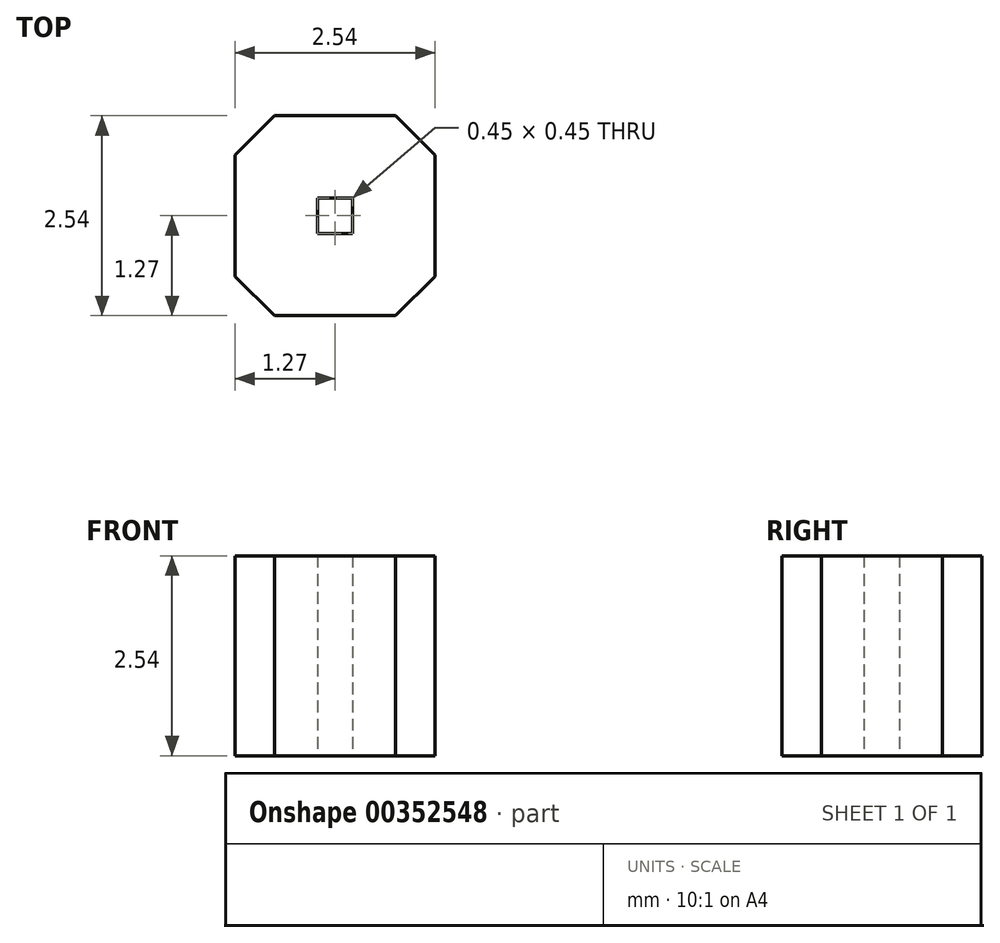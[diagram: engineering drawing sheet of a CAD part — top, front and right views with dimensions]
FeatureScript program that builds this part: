
annotation { "Feature Type Name" : "Feature", "Feature Type Description" : "" }
export const myFeature = defineFeature(function(context is Context, id is Id, definition is map)
    precondition{}
    {
        {
            var Q0;
            Q0=qCreatedBy(makeId("Top.planeOp"),FACE);
            var sketch = newSketch(context, id + "F0", { "sketchPlane" : qUnion([Q0])});
            skLineSegment(sketch, "E0", {"start": v(0, 1.27) * mm, "end": v(0.77, 1.27) * mm});
            skLineSegment(sketch, "E1", {"start": v(0.77, 1.27) * mm, "end": v(1.27, 0.77) * mm});
            skLineSegment(sketch, "E2", {"start": v(1.27, 0.77) * mm, "end": v(1.27, 0) * mm});
            skLineSegment(sketch, "E3", {"start": v(0.77, 1.27) * mm, "end": v(1.27, 1.27) * mm, "construction": true});
            skLineSegment(sketch, "E4", {"start": v(1.27, 1.27) * mm, "end": v(1.27, 0.77) * mm, "construction": true});
            skLineSegment(sketch, "E5", {"start": v(0, 0) * mm, "end": v(0, 1.27) * mm, "construction": true});
            skLineSegment(sketch, "E6", {"start": v(0, 0) * mm, "end": v(1.27, 0) * mm, "construction": true});
            skLineSegment(sketch, "E7.MirrorCS", {"start": v(-0.77, 1.27) * mm, "end": v(-1.27, 0.77) * mm});
            skLineSegment(sketch, "E8.MirrorCS", {"start": v(0, 1.27) * mm, "end": v(-0.77, 1.27) * mm});
            skLineSegment(sketch, "E9.MirrorCS", {"start": v(-1.27, 0.77) * mm, "end": v(-1.27, 0) * mm});
            skLineSegment(sketch, "E10.MirrorCS", {"start": v(-0.77, 1.27) * mm, "end": v(-1.27, 1.27) * mm, "construction": true});
            skLineSegment(sketch, "E11.MirrorCS", {"start": v(-1.27, 1.27) * mm, "end": v(-1.27, 0.77) * mm, "construction": true});
            skLineSegment(sketch, "E12.MirrorCS", {"start": v(0, -1.27) * mm, "end": v(0.77, -1.27) * mm});
            skLineSegment(sketch, "E13.MirrorCS", {"start": v(0.77, -1.27) * mm, "end": v(1.27, -0.77) * mm});
            skLineSegment(sketch, "E14.MirrorCS", {"start": v(1.27, -0.77) * mm, "end": v(1.27, 0) * mm});
            skLineSegment(sketch, "E15.MirrorCS", {"start": v(0.77, -1.27) * mm, "end": v(1.27, -1.27) * mm, "construction": true});
            skLineSegment(sketch, "E16.MirrorCS", {"start": v(1.27, -1.27) * mm, "end": v(1.27, -0.77) * mm, "construction": true});
            skLineSegment(sketch, "E17.MirrorCS", {"start": v(-0.77, -1.27) * mm, "end": v(-1.27, -1.27) * mm, "construction": true});
            skLineSegment(sketch, "E18.MirrorCS", {"start": v(-1.27, -1.27) * mm, "end": v(-1.27, -0.77) * mm, "construction": true});
            skLineSegment(sketch, "E19.MirrorCS", {"start": v(-1.27, -0.77) * mm, "end": v(-1.27, 0) * mm});
            skLineSegment(sketch, "E20.MirrorCS", {"start": v(0, -1.27) * mm, "end": v(-0.77, -1.27) * mm});
            skLineSegment(sketch, "E21.MirrorCS", {"start": v(-0.77, -1.27) * mm, "end": v(-1.27, -0.77) * mm});
            skLineSegment(sketch, "E22.bottom", {"start": v(0.23, 0.23) * mm, "end": v(-0.23, 0.23) * mm});
            skLineSegment(sketch, "E22.top", {"start": v(0.23, -0.23) * mm, "end": v(-0.23, -0.22) * mm});
            skLineSegment(sketch, "E22.left", {"start": v(0.23, 0.23) * mm, "end": v(0.23, -0.23) * mm});
            skLineSegment(sketch, "E22.right", {"start": v(-0.23, 0.23) * mm, "end": v(-0.23, -0.23) * mm});
            skPoint(sketch, "E22.middle", {"position": v(0, 0) * mm});
            skSolve(sketch);
        }
        {
            var Q0;
            Q0 = qSketchRegion(id + "F0", true);
            extrude(context, id + "F1", {"entities" : qUnion([Q0]), "depth" : 2.54 * mm});
        }
    });
